# Revit family: Cabinet_Wenger_UltraStor_41
name_source: partatom
category: Furniture
revit_build: Autodesk Revit 2015 (Build: 20140606_1530(x64)
units: mm (PartAtom-declared; Revit-internal decimal feet)

## types (4) — shared parameters
Assembly Code = E2010200
Cabinet Height = 7' - 1 5/8"
Construction Details = http://www.arcat.com
Green Building-LEED = http://www.arcat.com
Installed Depth = 4' - 0 1/4"
Keynote = 12 35 83
Manufacturer = Wenger Corporation
Manufacturer Fax = (507) 455-4258
Manufacturer Website = https://www.wengercorp.com
Model = #41
Product Data = http://www.arcat.com
Rear Panel Thickness = 0' - 0 3/4"
Revision = R1_2018-04
Sales Information = https://www.wengercorp.com
Specification = http://www.arcat.com
Toe Kick Depth = 0' - 2 1/4"
Toe Kick Height = 0' - 4"
URL = https://www.wengercorp.com
zero-valued in all types: Cost

## per-type parameters (varying)
| type | Cabinet Width | Description | Door Style | End Panel Material | HasDoors |
| Wood Door | 4' - 0 1/4" | Wenger UltraStor Cabinet #41 - Comp Wood Doors | Door_FullHt : Solid Door | Wenger Cherry (Use Cherry Edge Band Only) | Yes |
| Grille Door | 4' - 0 1/4" | Wenger UltraStor Cabinet #41 - Comp Grille Doors | Door_FullHt : Bars | Wenger Cherry (Use Cherry Edge Band Only) | Yes |
| No Door | 4' - 0 1/2" | Wenger UltraStor Cabinet #41 - No Doors | Door_FullHt : Solid Door | Wenger Cherry (Use Cherry Edge Band Only) | No |
| Waterfall Grille Door | 4' - 0 1/2" | Wenger UltraStor Cabinet #41 - Comp Waterfall Grille Doors | Door_FullHt : Waterfall | <By Category> | Yes |

## geometry (parser evidence)
native form markers: Blend x16, Sweep x17
no freeform markers — native parametric forms only
